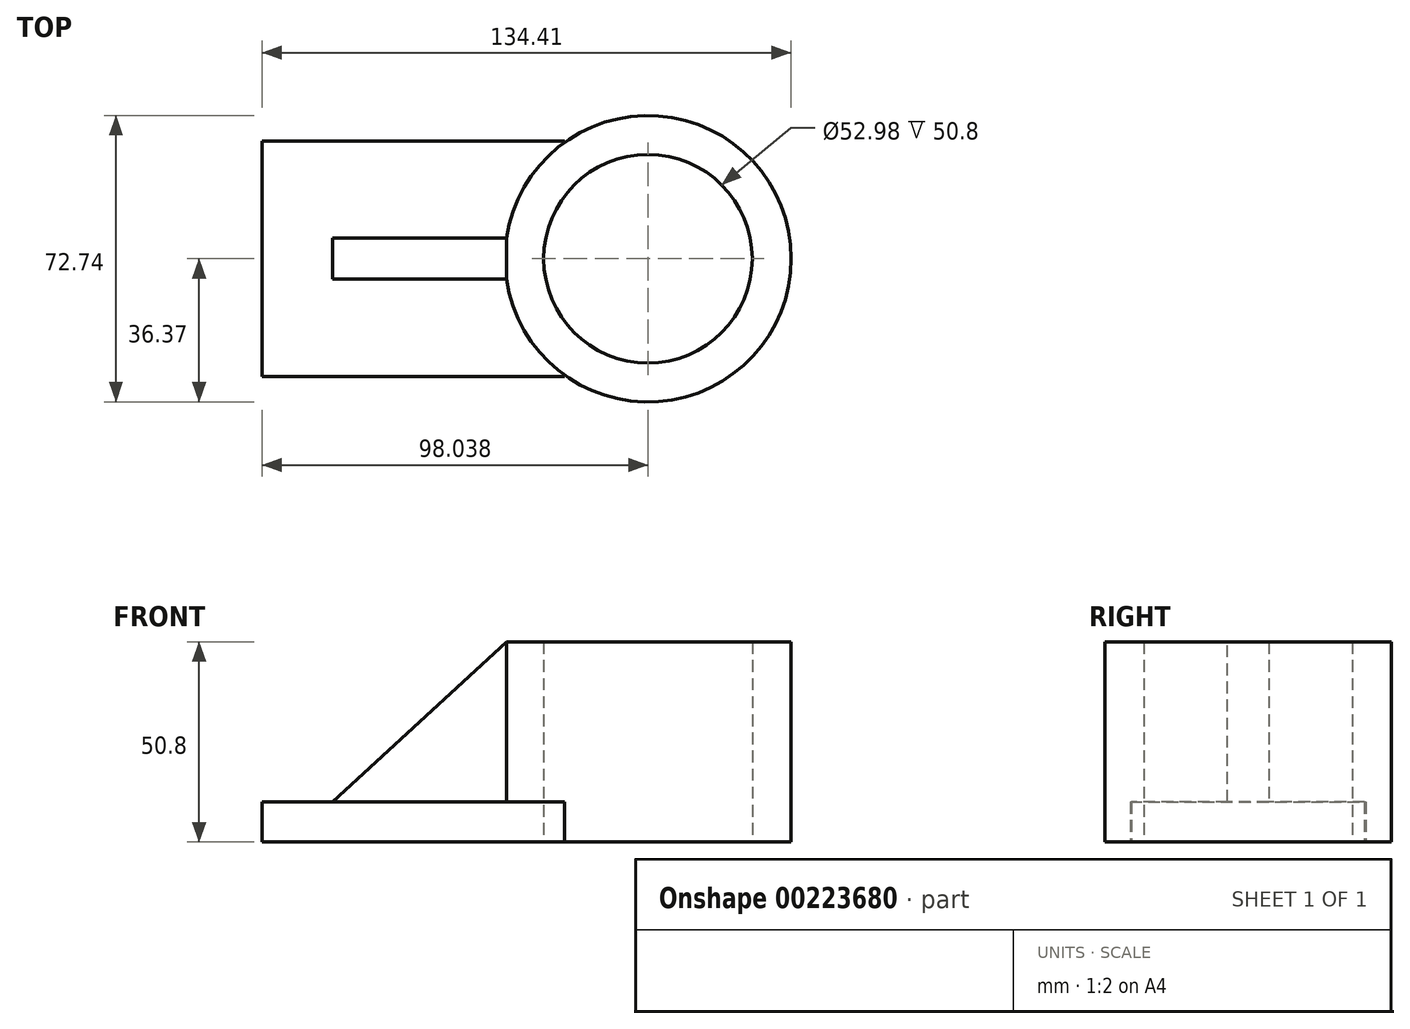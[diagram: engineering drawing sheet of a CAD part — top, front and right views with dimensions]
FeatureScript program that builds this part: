
annotation { "Feature Type Name" : "Feature", "Feature Type Description" : "" }
export const myFeature = defineFeature(function(context is Context, id is Id, definition is map)
    precondition{}
    {
        {
            var Q0;
            Q0=qCreatedBy(makeId("Top.planeOp"),FACE);
            var sketch = newSketch(context, id + "F0", { "sketchPlane" : qUnion([Q0])});
            skLineSegment(sketch, "E0.bottom", {"start": v(-38.44, -29.95) * mm, "end": v(38.44, -29.95) * mm});
            skLineSegment(sketch, "E0.top", {"start": v(-38.44, 29.95) * mm, "end": v(38.44, 29.95) * mm});
            skLineSegment(sketch, "E0.left", {"start": v(-38.44, -29.95) * mm, "end": v(-38.44, 29.95) * mm});
            skLineSegment(sketch, "E0.right", {"start": v(38.44, -29.95) * mm, "end": v(38.44, -29.58) * mm});
            skPoint(sketch, "E0.middle", {"position": v(0, 0) * mm});
            skCircle(sketch, "E1", {"center": v(59.6, 0) * mm, "radius": 36.37 * mm});
            skPoint(sketch, "E1.centerSnap0", {"position": v(38.44, 0) * mm});
            skLineSegment(sketch, "E2.trimOffspring", {"start": v(38.44, 29.58) * mm, "end": v(38.44, 29.95) * mm});
            skCircle(sketch, "E3", {"center": v(59.6, 0) * mm, "radius": 26.49 * mm});
            skSolve(sketch);
        }
        {
            var Q0;
            Q0=makeQuery(id+"F0.imprint","IMPRINT",FACE,{"disambiguationData":[TD([[makeQuery(id+"F0.imprint","IMPRINT",EDGE,{"derivedFrom":sQuery(id+"F0.wireOp",EDGE,"E0.bottom")}),1.0]])]});
            extrude(context, id + "F1", {"entities" : qUnion([Q0]), "depth" : 10.16 * mm});
        }
        {
            var Q0;
            Q0=makeQuery(id+"F0.imprint","IMPRINT",FACE,{"disambiguationData":[TD([[makeQuery(id+"F0.imprint","IMPRINT",EDGE,{"derivedFrom":sQuery(id+"F0.wireOp",EDGE,"E3")}),-1.0]])]});
            extrude(context, id + "F2", {"entities" : qUnion([Q0]), "operationType" : NewBodyOperationType.ADD, "depth" : 50.8 * mm});
        }
        {
            var Q0;
            Q0=makeQuery(id+"F1.opExtrude","CAP_FACE",FACE,{"disambiguationData":[OSD([sQuery(id+"F0.wireOp",EDGE,"E0.bottom"),sQuery(id+"F0.wireOp",EDGE,"E0.top"),sQuery(id+"F0.wireOp",EDGE,"E0.left"),sQuery(id+"F0.wireOp",EDGE,"E0.right"),sQuery(id+"F0.wireOp",EDGE,"E1"),sQuery(id+"F0.wireOp",EDGE,"E2.trimOffspring")])],"isStart":false});
            var sketch = newSketch(context, id + "F3", { "sketchPlane" : qUnion([Q0])});
            skLineSegment(sketch, "E4.bottom", {"start": v(-20.51, 5.21) * mm, "end": v(24.78, 5.21) * mm});
            skLineSegment(sketch, "E4.top", {"start": v(-20.51, -5.21) * mm, "end": v(24.78, -5.21) * mm});
            skLineSegment(sketch, "E4.left", {"start": v(-20.51, 5.21) * mm, "end": v(-20.51, -5.21) * mm});
            skLineSegment(sketch, "E4.right", {"start": v(24.78, 5.21) * mm, "end": v(24.78, -5.21) * mm});
            skPoint(sketch, "E4.middle", {"position": v(2.14, 0) * mm});
            skSolve(sketch);
        }
        {
            var Q0;
            Q0 = qSketchRegion(id + "F3", true);
            extrude(context, id + "F4", {"entities" : qUnion([Q0]), "operationType" : NewBodyOperationType.ADD, "depth" : 40.64 * mm});
        }
        {
            var Q0;
            Q0=makeQuery(id+"F4.opExtrude","SWEPT_FACE",FACE,{"disambiguationData":[OSD([sQuery(id+"F3.wireOp",EDGE,"E4.top")])]});
            var sketch = newSketch(context, id + "F5", { "sketchPlane" : qUnion([Q0])});
            skLineSegment(sketch, "E5", {"start": v(-20.51, 10.16) * mm, "end": v(23.6, 50.8) * mm});
            skLineSegment(sketch, "E6", {"start": v(23.6, 50.8) * mm, "end": v(-20.51, 50.8) * mm});
            skLineSegment(sketch, "E7", {"start": v(-20.51, 50.8) * mm, "end": v(-20.51, 10.16) * mm});
            skSolve(sketch);
        }
        {
            var Q0;
            Q0=makeQuery(id+"F5.imprint","IMPRINT",FACE,{"disambiguationData":[TD([[makeQuery(id+"F5.imprint","IMPRINT",EDGE,{"derivedFrom":sQuery(id+"F5.wireOp",EDGE,"E5")}),1.0]])]});
            extrude(context, id + "F6", {"entities" : qUnion([Q0]), "operationType" : NewBodyOperationType.REMOVE, "endBound" : BoundingType.THROUGH_ALL, "oppositeDirection" : true, "depth" : 25.4 * mm});
        }
    });
